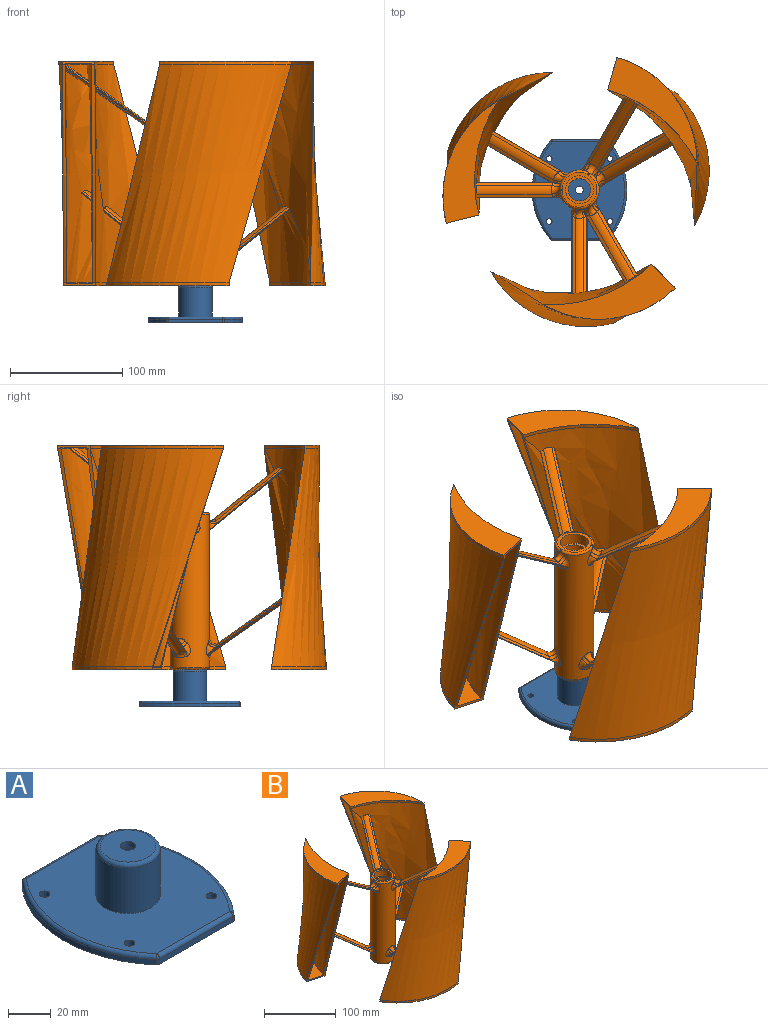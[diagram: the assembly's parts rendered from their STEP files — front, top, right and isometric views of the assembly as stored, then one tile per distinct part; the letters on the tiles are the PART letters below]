
ASSEMBLY  parts=2 mates=1
PART A: 29 faces, bbox 95.6x95.9x33 mm
  f0: cylinder r=67.27mm len=88.64mm, axis (0,0,-1), area 290.3mm2, adj f9,f15,f19,f21
  f1: plane 48.2x3mm, normal (0,-1,0), area 144.6mm2, adj f9,f10,f14,f15
  f2: cylinder r=67.27mm len=88.64mm, axis (0,0,-1), area 290.3mm2, adj f9,f10,f12,f13
  f3: cylinder r=2.5mm len=5mm, axis (0,0,-1), area 78.5mm2, adj f8,f9
  f4: cylinder r=2.5mm len=5mm, axis (0,0,-1), area 78.5mm2, adj f8,f9
  f5: cylinder r=2.5mm len=5mm, axis (0,0,-1), area 78.5mm2, adj f8,f9
  f6: plane 48.2x3mm, normal (0,1,0), area 144.6mm2, adj f9,f12,f18,f21
  f7: cylinder r=2.5mm len=5mm, axis (0,0,-1), area 78.5mm2, adj f8,f9
  f8: plane 86x80.54mm, normal (0,0,1), area 5265.2mm2, adj f3,f4,f5,f7,f13,f14,f18,f19
  f9: plane 90x84.54mm, normal (0,0,-1), area 5846.1mm2, adj f0,f1,f2,f3,f4,f5,f6,f7
  f10: cylinder r=2mm len=3mm, axis (0,0,-1), area 5.1mm2, adj f1,f2,f9,f11
  f11: sphere r=2mm, area 3.4mm2, adj f10,f13,f14
  f12: cylinder r=2mm len=3mm, axis (0,0,-1), area 5.1mm2, adj f2,f6,f9,f16
  f13: torus R=65.27mm, axis (0,0,1), area 300.7mm2, adj f2,f8,f11,f16
  f14: cylinder r=2mm len=48.2mm, axis (-1,0,0), area 151.4mm2, adj f1,f8,f11,f17
  f15: cylinder r=2mm len=3mm, axis (0,0,-1), area 5.1mm2, adj f0,f1,f9,f17
  f16: sphere r=2mm, area 3.4mm2, adj f12,f13,f18
  f17: sphere r=2mm, area 3.4mm2, adj f14,f15,f19
  f18: cylinder r=2mm len=48.2mm, axis (1,0,0), area 151.4mm2, adj f6,f8,f16,f20
  f19: torus R=65.27mm, axis (0,0,1), area 300.7mm2, adj f0,f8,f17,f20
  f20: sphere r=2mm, area 3.4mm2, adj f18,f19,f21
  f21: cylinder r=2mm len=3mm, axis (0,0,-1), area 5.1mm2, adj f0,f6,f9,f20
  f22: cylinder r=15mm len=30mm, axis (0,0,-1), area 2450.4mm2, adj f8,f27
  f23: plane 20x20mm, normal (0,0,-1), area 275.7mm2, adj f24,f26
  f24: cylinder r=3.5mm len=7mm, axis (0,0,-1), area 66mm2, adj f23,f25
  f25: plane 26x26mm, normal (0,0,1), area 492.4mm2, adj f24,f27
  f26: cylinder r=10mm len=25mm, axis (0,0,-1), area 1570.8mm2, adj f23,f28
  f27: torus R=13mm, axis (0,0,1), area 281.7mm2, adj f22,f25
  f28: torus R=15mm, axis (0,0,1), area 583.1mm2, adj f9,f26
PART B: 222 faces, bbox 237.7x239.8x200 mm
  f0: cylinder r=95.25mm len=64.02mm, axis (0,0,1), area 75.9mm2, adj f2,f69,f70,f143,f145
  f1: cylinder r=0.3mm len=20.23mm, axis (0.41,0.71,0.57), area 19.3mm2, adj f2,f3,f61,f69
  f2: bspline ~194x133.89mm, area 20844.4mm2, adj f0,f1,f3,f4,f5,f6,f7,f24
  f3: plane 21.15x17.34mm, normal (0.6,0.26,-0.75), area 79.2mm2, adj f1,f2,f4,f61
  f4: cylinder r=10mm len=24.72mm, axis (0.41,0.71,0.57), area 232.5mm2, adj f2,f3,f6,f61
  f5: cylinder r=0.3mm len=21.63mm, axis (-0.41,-0.71,-0.57), area 20.7mm2, adj f2,f6,f7,f61
  f6: plane 22.19x18.25mm, normal (-0.08,0.65,-0.75), area 83.6mm2, adj f2,f4,f5,f61
  f7: plane 22.03x18.04mm, normal (-0.6,-0.26,0.75), area 83.3mm2, adj f2,f5,f61,f70,f142,f145
  f8: cylinder r=95.25mm len=74.67mm, axis (0,0,1), area 75.9mm2, adj f10,f96,f98,f106,f107
  f9: cylinder r=0.3mm len=20.23mm, axis (0.41,-0.71,0.57), area 19.3mm2, adj f10,f11,f91,f107
  f10: bspline ~194x152.48mm, area 20844.4mm2, adj f8,f9,f11,f12,f13,f14,f15,f25
  f11: plane 21.07x17.34mm, normal (-0.08,-0.65,-0.75), area 79.2mm2, adj f9,f10,f12,f91
  f12: cylinder r=10mm len=24.72mm, axis (0.41,-0.71,0.57), area 232.5mm2, adj f10,f11,f13,f91
  f13: plane 22.24x18.25mm, normal (0.6,-0.26,-0.75), area 83.6mm2, adj f10,f12,f14,f91
  f14: cylinder r=0.3mm len=21.63mm, axis (-0.41,0.71,-0.57), area 20.7mm2, adj f10,f13,f15,f91
  f15: plane 22.02x18.04mm, normal (0.08,0.65,0.75), area 83.3mm2, adj f10,f14,f91,f95,f98,f106
  f16: cylinder r=95.25mm len=65.31mm, axis (0,0,1), area 75.9mm2, adj f18,f39,f40,f157,f159
  f17: cylinder r=0.3mm len=23.34mm, axis (-0.82,0,0.57), area 19.3mm2, adj f18,f19,f30,f40
  f18: bspline ~194x130.22mm, area 20844.4mm2, adj f16,f17,f19,f20,f21,f22,f23,f29
  f19: plane 23.06x17.34mm, normal (-0.53,0.39,-0.75), area 79.2mm2, adj f17,f18,f20,f30
  f20: cylinder r=10mm len=24.46mm, axis (-0.82,0,0.57), area 232.5mm2, adj f18,f19,f22,f30
  f21: cylinder r=0.3mm len=24.96mm, axis (0.82,0,-0.57), area 20.7mm2, adj f18,f22,f23,f30
  f22: plane 24.29x18.25mm, normal (-0.53,-0.39,-0.75), area 83.6mm2, adj f18,f20,f21,f30
  f23: plane 24.29x18.04mm, normal (0.53,-0.39,0.75), area 83.3mm2, adj f18,f21,f30,f39,f156,f159
  f24: plane 17.77x14.45mm, normal (0.26,0.6,-0.75), area 65.3mm2, adj f2,f61,f63,f64
  f25: plane 19.09x14.45mm, normal (0.39,-0.53,-0.75), area 65.3mm2, adj f10,f91,f101,f103
  f26: bspline ~194x49.43mm, area 586mm2, adj f27,f30,f155,f162
  f27: bspline ~194x127.52mm, area 20025.6mm2, adj f26,f28,f41,f42,f43,f44,f45,f46
  f28: bspline ~194x134.86mm, area 24099.9mm2, adj f27,f29,f154,f161
  f29: bspline ~194x63.4mm, area 597.1mm2, adj f18,f28,f155,f162
  f30: bspline ~194x124.34mm, area 17988.6mm2, adj f17,f18,f19,f20,f21,f22,f23,f26
  f31: cylinder r=0.3mm len=17.06mm, axis (-0.71,0.41,0.57), area 16.3mm2, adj f18,f30,f32,f35
  f32: plane 17.45x14.57mm, normal (0.26,-0.6,0.75), area 64.9mm2, adj f18,f30,f31,f33
  f33: cylinder r=10mm len=19.9mm, axis (0.71,-0.41,-0.57), area 173.2mm2, adj f18,f30,f32,f37
  f34: cylinder r=10mm len=20.05mm, axis (0.71,-0.41,-0.57), area 175.2mm2, adj f18,f30,f35,f36
  f35: plane 17.49x14.45mm, normal (-0.65,-0.08,-0.75), area 65.3mm2, adj f18,f30,f31,f34
  f36: plane 15.72x12.82mm, normal (-0.26,0.6,-0.75), area 57.1mm2, adj f18,f30,f34,f38
  f37: plane 15.56x12.89mm, normal (0.65,0.08,0.75), area 56.7mm2, adj f18,f30,f33,f38
  f38: cylinder r=0.3mm len=14.5mm, axis (0.71,-0.41,-0.57), area 13.8mm2, adj f18,f30,f36,f37
  f39: cylinder r=10mm len=23.91mm, axis (-0.82,0,0.57), area 219.3mm2, adj f16,f23,f30,f40,f159
  f40: plane 23.01x17.47mm, normal (0.53,0.39,0.75), area 79mm2, adj f16,f17,f18,f30,f39
  f41: plane 68.26x49.15mm, normal (0.53,-0.39,0.75), area 234.1mm2, adj f27,f44,f48,f190
  f42: plane 73.31x51.94mm, normal (-0.53,-0.39,-0.75), area 251.9mm2, adj f27,f47,f48,f186
  f43: plane 68.73x49.48mm, normal (0.53,0.39,0.75), area 236.3mm2, adj f27,f44,f46,f187
  f44: cylinder r=10mm len=68.3mm, axis (-0.82,0,0.57), area 668.2mm2, adj f27,f41,f43,f189
  f45: plane 73.89x52.47mm, normal (-0.53,0.39,-0.75), area 254mm2, adj f27,f46,f47,f183
  f46: cylinder r=0.3mm len=74.69mm, axis (-0.82,0,0.57), area 61.7mm2, adj f27,f43,f45,f185
  f47: cylinder r=10mm len=73.33mm, axis (-0.82,0,0.57), area 718mm2, adj f27,f42,f45,f184
  f48: cylinder r=0.3mm len=73.92mm, axis (0.82,0,-0.57), area 61.1mm2, adj f27,f41,f42,f188
  f49: cylinder r=0.3mm len=65.06mm, axis (0.71,-0.41,-0.57), area 62.1mm2, adj f27,f50,f51,f208
  f50: plane 60.98x49.6mm, normal (0.65,0.08,0.75), area 237.3mm2, adj f27,f49,f53,f210
  f51: plane 65.52x52.79mm, normal (-0.26,0.6,-0.75), area 255.5mm2, adj f27,f49,f56,f207
  f52: plane 63.61x51.73mm, normal (-0.65,-0.08,-0.75), area 251.3mm2, adj f27,f55,f56,f211
  f53: cylinder r=10mm len=62.84mm, axis (0.71,-0.41,-0.57), area 667.7mm2, adj f27,f50,f54,f212
  f54: plane 59.04x48.95mm, normal (0.26,-0.6,0.75), area 233mm2, adj f27,f53,f55,f214
  f55: cylinder r=0.3mm len=63.73mm, axis (-0.71,0.41,0.57), area 60.8mm2, adj f27,f52,f54,f213
  f56: cylinder r=10mm len=67.38mm, axis (0.71,-0.41,-0.57), area 719.6mm2, adj f27,f51,f52,f209
  f57: bspline ~194x43.27mm, area 586mm2, adj f58,f61,f141,f148
  f58: bspline ~194x120.93mm, area 20025.6mm2, adj f57,f59,f71,f72,f73,f74,f75,f76
  f59: bspline ~194x149.79mm, area 24099.9mm2, adj f58,f60,f140,f147
  f60: bspline ~194x55.27mm, area 597.1mm2, adj f2,f59,f141,f148
  f61: bspline ~194x110.8mm, area 17988.6mm2, adj f1,f2,f3,f4,f5,f6,f7,f24
  f62: plane 17.64x14.57mm, normal (-0.65,0.08,0.75), area 64.9mm2, adj f2,f61,f63,f68
  f63: cylinder r=0.3mm len=17.06mm, axis (0.71,0.41,0.57), area 16.3mm2, adj f2,f24,f61,f62
  f64: cylinder r=10mm len=20.05mm, axis (-0.71,-0.41,-0.57), area 175.2mm2, adj f2,f24,f61,f67
  f65: cylinder r=0.3mm len=14.5mm, axis (-0.71,-0.41,-0.57), area 13.8mm2, adj f2,f61,f66,f67
  f66: plane 15.4x12.89mm, normal (-0.26,-0.6,0.75), area 56.7mm2, adj f2,f61,f65,f68
  f67: plane 15.47x12.82mm, normal (0.65,-0.08,-0.75), area 57.1mm2, adj f2,f61,f64,f65
  f68: cylinder r=10mm len=19.9mm, axis (-0.71,-0.41,-0.57), area 173.2mm2, adj f2,f61,f62,f66
  f69: plane 21.23x17.47mm, normal (0.08,-0.65,0.75), area 79mm2, adj f0,f1,f2,f61,f70
  f70: cylinder r=10mm len=24.25mm, axis (0.41,0.71,0.57), area 219.3mm2, adj f0,f7,f61,f69,f145
  f71: cylinder r=0.3mm len=64.7mm, axis (0.41,0.71,0.57), area 61.7mm2, adj f58,f77,f78,f176
  f72: cylinder r=0.3mm len=64.04mm, axis (-0.41,-0.71,-0.57), area 61.1mm2, adj f58,f75,f76,f181
  f73: cylinder r=10mm len=62.69mm, axis (0.41,0.71,0.57), area 668.2mm2, adj f58,f75,f77,f177
  f74: cylinder r=10mm len=67.04mm, axis (0.41,0.71,0.57), area 718mm2, adj f58,f76,f78,f180
  f75: plane 59.34x49.15mm, normal (-0.6,-0.26,0.75), area 234.1mm2, adj f58,f72,f73,f179
  f76: plane 63.87x51.94mm, normal (-0.08,0.65,-0.75), area 251.9mm2, adj f58,f72,f74,f182
  f77: plane 60.83x49.48mm, normal (0.08,-0.65,0.75), area 236.3mm2, adj f58,f71,f73,f175
  f78: plane 65.18x52.47mm, normal (0.6,0.26,-0.75), area 254mm2, adj f58,f71,f74,f178
  f79: cylinder r=10mm len=62.84mm, axis (-0.71,-0.41,-0.57), area 667.7mm2, adj f58,f82,f85,f191
  f80: plane 64.73x51.73mm, normal (0.26,0.6,-0.75), area 251.3mm2, adj f58,f81,f84,f196
  f81: cylinder r=0.3mm len=63.73mm, axis (0.71,0.41,0.57), area 60.8mm2, adj f58,f80,f82,f194
  f82: plane 60.17x48.95mm, normal (-0.65,0.08,0.75), area 233mm2, adj f58,f79,f81,f192
  f83: plane 64.93x52.79mm, normal (0.65,-0.08,-0.75), area 255.5mm2, adj f58,f84,f86,f197
  f84: cylinder r=10mm len=67.38mm, axis (-0.71,-0.41,-0.57), area 719.6mm2, adj f58,f80,f83,f198
  f85: plane 60.37x49.6mm, normal (-0.26,-0.6,0.75), area 237.3mm2, adj f58,f79,f86,f193
  f86: cylinder r=0.3mm len=65.06mm, axis (-0.71,-0.41,-0.57), area 62.1mm2, adj f58,f83,f85,f195
  f87: bspline ~194x43.9mm, area 586mm2, adj f88,f91,f94,f134
  f88: bspline ~194x143.44mm, area 20025.6mm2, adj f87,f89,f92,f108,f109,f110,f111,f112
  f89: bspline ~194x164.35mm, area 24099.9mm2, adj f88,f90,f93,f133
  f90: bspline ~194x56.1mm, area 597.1mm2, adj f10,f89,f94,f134
  f91: bspline ~194x135.76mm, area 17988.6mm2, adj f9,f10,f11,f12,f13,f14,f15,f25
  f92: cylinder r=128.97mm len=96.39mm, axis (0,0,1), area 317.9mm2, adj f88,f93,f94,f97
  f93: cylinder r=98.25mm len=117.3mm, axis (0,0,1), area 380.6mm2, adj f89,f92,f94,f97
  f94: plane 21.52x20.91mm, normal (0.72,0.7,0), area 66mm2, adj f87,f90,f92,f93,f95,f96,f97,f98
  f95: cylinder r=95.25mm len=19.95mm, axis (0,0,1), area 24mm2, adj f10,f15,f94,f98
  f96: cylinder r=131.97mm len=85.47mm, axis (0,0,1), area 95.2mm2, adj f8,f91,f94,f98
  f97: plane 117.3x49.3mm, normal (0,0,1), area 2266.2mm2, adj f92,f93,f94
  f98: plane 102.19x44.15mm, normal (0,0,-1), area 1598.7mm2, adj f8,f15,f94,f95,f96,f106
  f99: cylinder r=10mm len=18.89mm, axis (0,0.82,-0.57), area 173.2mm2, adj f10,f91,f100,f104
  f100: plane 16.64x12.89mm, normal (-0.39,0.53,0.75), area 56.7mm2, adj f10,f91,f99,f105
  f101: cylinder r=0.3mm len=19.69mm, axis (0,-0.82,0.57), area 16.3mm2, adj f10,f25,f91,f104
  f102: plane 16.86x12.82mm, normal (-0.39,-0.53,-0.75), area 57.1mm2, adj f10,f91,f103,f105
  f103: cylinder r=10mm len=19.06mm, axis (0,0.82,-0.57), area 175.2mm2, adj f10,f25,f91,f102
  f104: plane 19.06x14.57mm, normal (0.39,0.53,0.75), area 64.9mm2, adj f10,f91,f99,f101
  f105: cylinder r=0.3mm len=16.73mm, axis (0,0.82,-0.57), area 13.8mm2, adj f10,f91,f100,f102
  f106: cylinder r=10mm len=24.25mm, axis (0.41,-0.71,0.57), area 219.3mm2, adj f8,f15,f91,f98,f107
  f107: plane 20.88x17.47mm, normal (-0.6,0.26,0.75), area 79mm2, adj f8,f9,f10,f91,f106
  f108: plane 60.42x49.15mm, normal (0.08,0.65,0.75), area 234.1mm2, adj f88,f113,f114,f172
  f109: plane 64.79x51.94mm, normal (0.6,-0.26,-0.75), area 251.9mm2, adj f88,f113,f115,f168
  f110: plane 60.01x49.48mm, normal (-0.6,0.26,0.75), area 236.3mm2, adj f88,f112,f114,f173
  f111: plane 64.53x52.47mm, normal (-0.08,-0.65,-0.75), area 254mm2, adj f88,f112,f115,f169
  f112: cylinder r=0.3mm len=64.7mm, axis (0.41,-0.71,0.57), area 61.7mm2, adj f88,f110,f111,f171
  f113: cylinder r=0.3mm len=64.04mm, axis (-0.41,0.71,-0.57), area 61.1mm2, adj f88,f108,f109,f170
  f114: cylinder r=10mm len=62.69mm, axis (0.41,-0.71,0.57), area 668.2mm2, adj f88,f108,f110,f174
  f115: cylinder r=10mm len=67.04mm, axis (0.41,-0.71,0.57), area 718mm2, adj f88,f109,f111,f167
  f116: cylinder r=0.3mm len=75.11mm, axis (0,0.82,-0.57), area 62.1mm2, adj f88,f121,f122,f205
  f117: plane 67.98x48.95mm, normal (0.39,0.53,0.75), area 233mm2, adj f88,f120,f123,f199
  f118: plane 73.24x51.73mm, normal (0.39,-0.53,-0.75), area 251.3mm2, adj f88,f119,f120,f202
  f119: cylinder r=10mm len=73.72mm, axis (0,0.82,-0.57), area 719.6mm2, adj f88,f118,f122,f204
  f120: cylinder r=0.3mm len=73.57mm, axis (0,-0.82,0.57), area 60.8mm2, adj f88,f117,f118,f200
  f121: plane 69.09x49.6mm, normal (-0.39,0.53,0.75), area 237.3mm2, adj f88,f116,f123,f203
  f122: plane 74.35x52.79mm, normal (-0.39,-0.53,-0.75), area 255.5mm2, adj f88,f116,f119,f206
  f123: cylinder r=10mm len=68.48mm, axis (0,0.82,-0.57), area 667.7mm2, adj f88,f117,f121,f201
  f124: plane 25x25mm, normal (0,0,1), area 176.7mm2, adj f125,f131
  f125: cylinder r=12.5mm len=25mm, axis (0,0,1), area 785.4mm2, adj f124,f126
  f126: plane 31x31mm, normal (0,0,1), area 263.9mm2, adj f125,f215,f216,f217,f218,f219,f220
  f127: plane 25x25mm, normal (0,0,-1), area 176.7mm2, adj f129,f131
  f128: plane 31x31mm, normal (0,0,-1), area 263.9mm2, adj f129,f221
  f129: cylinder r=12.5mm len=25mm, axis (0,0,-1), area 785.4mm2, adj f127,f128
  f130: cylinder r=17.5mm len=136mm, axis (0,0,-1), area 13436.7mm2, adj f167,f168,f169,f170,f171,f172,f173,f174
  f131: cylinder r=10mm len=120mm, axis (0,0,-1), area 7539.8mm2, adj f124,f127
  f132: cylinder r=128.97mm len=101.63mm, axis (0,0,-1), area 317.9mm2, adj f88,f133,f134,f137
  f133: cylinder r=98.25mm len=108.98mm, axis (0,0,-1), area 380.6mm2, adj f89,f132,f134,f137
  f134: plane 29.09x7.35mm, normal (0.97,0.24,0), area 66mm2, adj f87,f90,f132,f133,f135,f136,f137,f138
  f135: cylinder r=95.25mm len=98.47mm, axis (0,0,-1), area 110.2mm2, adj f10,f134,f136,f138
  f136: cylinder r=131.97mm len=92.6mm, axis (0,0,-1), area 95.2mm2, adj f91,f134,f135,f138
  f137: plane 108.98x48.83mm, normal (0,0,-1), area 2266.2mm2, adj f132,f133,f134
  f138: plane 98.47x36.72mm, normal (0,0,1), area 1608.4mm2, adj f134,f135,f136
  f139: cylinder r=128.97mm len=79.64mm, axis (0,0,1), area 317.9mm2, adj f58,f140,f141,f144
  f140: cylinder r=98.25mm len=94.19mm, axis (0,0,1), area 380.6mm2, adj f59,f139,f141,f144
  f141: plane 28.86x8.18mm, normal (-0.96,0.27,0), area 66mm2, adj f57,f60,f139,f140,f142,f143,f144,f145
  f142: cylinder r=95.25mm len=22.84mm, axis (0,0,1), area 24mm2, adj f2,f7,f141,f145
  f143: cylinder r=131.97mm len=74.91mm, axis (0,0,1), area 95.2mm2, adj f0,f61,f141,f145
  f144: plane 94.19x79.64mm, normal (0,0,1), area 2266.2mm2, adj f139,f140,f141
  f145: plane 78.53x74.91mm, normal (0,0,-1), area 1598.7mm2, adj f0,f7,f70,f141,f142,f143
  f146: cylinder r=128.97mm len=96.39mm, axis (0,0,-1), area 317.9mm2, adj f58,f147,f148,f151
  f147: cylinder r=98.25mm len=117.3mm, axis (0,0,-1), area 380.6mm2, adj f59,f146,f148,f151
  f148: plane 21.52x20.91mm, normal (-0.7,0.72,0), area 66mm2, adj f57,f60,f146,f147,f149,f150,f151,f152
  f149: cylinder r=95.25mm len=102.19mm, axis (0,0,-1), area 110.2mm2, adj f2,f148,f150,f152
  f150: cylinder r=131.97mm len=85.47mm, axis (0,0,-1), area 95.2mm2, adj f61,f148,f149,f152
  f151: plane 117.3x49.3mm, normal (0,0,-1), area 2266.2mm2, adj f146,f147,f148
  f152: plane 102.19x44.15mm, normal (0,0,1), area 1608.4mm2, adj f148,f149,f150
  f153: cylinder r=128.97mm len=101.63mm, axis (0,0,1), area 317.9mm2, adj f27,f154,f155,f158
  f154: cylinder r=98.25mm len=108.98mm, axis (0,0,1), area 380.6mm2, adj f28,f153,f155,f158
  f155: plane 29.09x7.35mm, normal (0.24,-0.97,0), area 66mm2, adj f26,f29,f153,f154,f156,f157,f158,f159
  f156: cylinder r=95.25mm len=24.7mm, axis (0,0,1), area 24mm2, adj f18,f23,f155,f159
  f157: cylinder r=131.97mm len=92.6mm, axis (0,0,1), area 95.2mm2, adj f16,f30,f155,f159
  f158: plane 108.98x48.83mm, normal (0,0,1), area 2266.2mm2, adj f153,f154,f155
  f159: plane 98.47x36.72mm, normal (0,0,-1), area 1598.7mm2, adj f16,f23,f39,f155,f156,f157
  f160: cylinder r=128.97mm len=79.64mm, axis (0,0,-1), area 317.9mm2, adj f27,f161,f162,f165
  f161: cylinder r=98.25mm len=94.19mm, axis (0,0,-1), area 380.6mm2, adj f28,f160,f162,f165
  f162: plane 28.86x8.18mm, normal (-0.27,-0.96,0), area 66mm2, adj f26,f29,f160,f161,f163,f164,f165,f166
  f163: cylinder r=95.25mm len=78.53mm, axis (0,0,-1), area 110.2mm2, adj f18,f162,f164,f166
  f164: cylinder r=131.97mm len=74.91mm, axis (0,0,-1), area 95.2mm2, adj f30,f162,f163,f166
  f165: plane 94.19x79.64mm, normal (0,0,-1), area 2266.2mm2, adj f160,f161,f162
  f166: plane 78.53x74.91mm, normal (0,0,1), area 1608.4mm2, adj f162,f163,f164
  f167: bspline ~10.35x7.26mm, area 40.3mm2, adj f115,f130,f168,f169
  f168: bspline ~4.51x3.83mm, area 11.4mm2, adj f109,f130,f167,f170
  f169: bspline ~4.51x3.76mm, area 11.4mm2, adj f111,f130,f167,f171
  f170: bspline ~12.62x9.14mm, area 51.4mm2, adj f113,f130,f168,f172
  f171: bspline ~12.62x7.4mm, area 51.4mm2, adj f112,f130,f169,f173
  f172: bspline ~8.4x5.98mm, area 29.5mm2, adj f108,f130,f170,f174
  f173: bspline ~6.67x6.4mm, area 29.5mm2, adj f110,f130,f171,f174
  f174: bspline ~13.03x11.72mm, area 79mm2, adj f114,f130,f172,f173,f217
  f175: bspline ~8.4x5.98mm, area 29.5mm2, adj f77,f130,f176,f177
  f176: bspline ~12.62x9.13mm, area 51.4mm2, adj f71,f130,f175,f178
  f177: bspline ~13.03x11.72mm, area 79mm2, adj f73,f130,f175,f179,f216
  f178: bspline ~4.51x3.83mm, area 11.4mm2, adj f78,f130,f176,f180
  f179: bspline ~6.67x6.4mm, area 29.5mm2, adj f75,f130,f177,f181
  f180: bspline ~10.35x7.26mm, area 40.3mm2, adj f74,f130,f178,f182
  f181: bspline ~12.62x7.4mm, area 51.4mm2, adj f72,f130,f179,f182
  f182: bspline ~4.51x3.76mm, area 11.4mm2, adj f76,f130,f180,f181
  f183: bspline ~4.51x2.88mm, area 11.4mm2, adj f45,f130,f184,f185
  f184: bspline ~10.63x5.06mm, area 40.3mm2, adj f47,f130,f183,f186
  f185: bspline ~12.62x9.03mm, area 51.4mm2, adj f46,f130,f183,f187
  f186: bspline ~4.51x2.88mm, area 11.4mm2, adj f42,f130,f184,f188
  f187: bspline ~8.15x5.98mm, area 29.5mm2, adj f43,f130,f185,f189
  f188: bspline ~12.62x9.03mm, area 51.4mm2, adj f48,f130,f186,f190
  f189: bspline ~11.73x9.61mm, area 79mm2, adj f44,f130,f187,f190,f220
  f190: bspline ~8.15x5.98mm, area 29.5mm2, adj f41,f130,f188,f189
  f191: bspline ~13.03x11.72mm, area 79mm2, adj f79,f130,f192,f193
  f192: bspline ~8.4x5.98mm, area 29.5mm2, adj f82,f130,f191,f194
  f193: bspline ~6.67x6.4mm, area 29.5mm2, adj f85,f130,f191,f195
  f194: bspline ~12.62x9.13mm, area 51.4mm2, adj f81,f130,f192,f196
  f195: bspline ~12.62x7.4mm, area 51.4mm2, adj f86,f130,f193,f197
  f196: bspline ~4.51x3.83mm, area 11.4mm2, adj f80,f130,f194,f198
  f197: bspline ~4.51x3.76mm, area 11.4mm2, adj f83,f130,f195,f198
  f198: bspline ~10.35x7.26mm, area 40.3mm2, adj f84,f130,f196,f197
  f199: bspline ~8.15x5.98mm, area 29.5mm2, adj f117,f130,f200,f201
  f200: bspline ~12.62x9.03mm, area 51.4mm2, adj f120,f130,f199,f202
  f201: bspline ~11.73x9.61mm, area 79mm2, adj f123,f130,f199,f203
  f202: bspline ~4.51x2.88mm, area 11.4mm2, adj f118,f130,f200,f204
  f203: bspline ~8.15x5.98mm, area 29.5mm2, adj f121,f130,f201,f205
  f204: bspline ~10.63x5.06mm, area 40.3mm2, adj f119,f130,f202,f206
  f205: bspline ~12.62x9.03mm, area 51.4mm2, adj f116,f130,f203,f206
  f206: bspline ~4.51x2.88mm, area 11.4mm2, adj f122,f130,f204,f205
  f207: bspline ~4.51x3.83mm, area 11.4mm2, adj f51,f130,f208,f209
  f208: bspline ~12.62x9.14mm, area 51.4mm2, adj f49,f130,f207,f210
  f209: bspline ~10.35x7.26mm, area 40.3mm2, adj f56,f130,f207,f211
  f210: bspline ~8.4x5.98mm, area 29.5mm2, adj f50,f130,f208,f212
  f211: bspline ~4.51x3.76mm, area 11.4mm2, adj f52,f130,f209,f213
  f212: bspline ~13.03x11.72mm, area 79mm2, adj f53,f130,f210,f214
  f213: bspline ~12.62x7.4mm, area 51.4mm2, adj f55,f130,f211,f214
  f214: bspline ~6.67x6.4mm, area 29.5mm2, adj f54,f130,f212,f213
  f215: torus R=15.5mm, axis (0,0,1), area 106.4mm2, adj f126,f130,f216,f217
  f216: bspline ~4.27x3.66mm, area 4mm2, adj f126,f177,f215,f218
  f217: bspline ~4.27x3.66mm, area 4mm2, adj f126,f174,f215,f219
  f218: torus R=15.5mm, axis (0,0,1), area 106.4mm2, adj f126,f130,f216,f220
  f219: torus R=15.5mm, axis (0,0,1), area 106.4mm2, adj f126,f130,f217,f220
  f220: bspline ~3.95x2.09mm, area 4mm2, adj f126,f189,f218,f219
  f221: torus R=15.5mm, axis (0,0,1), area 331.1mm2, adj f128,f130
PLACE A t=(-7.73,8.13,-29.68)mm
PLACE B t=(-7.73,8.13,3.32)mm
MATE fastened B.f130 <-> A.f22  axis (0,0,-1) through (-7.73,8.13,3.32)mm
